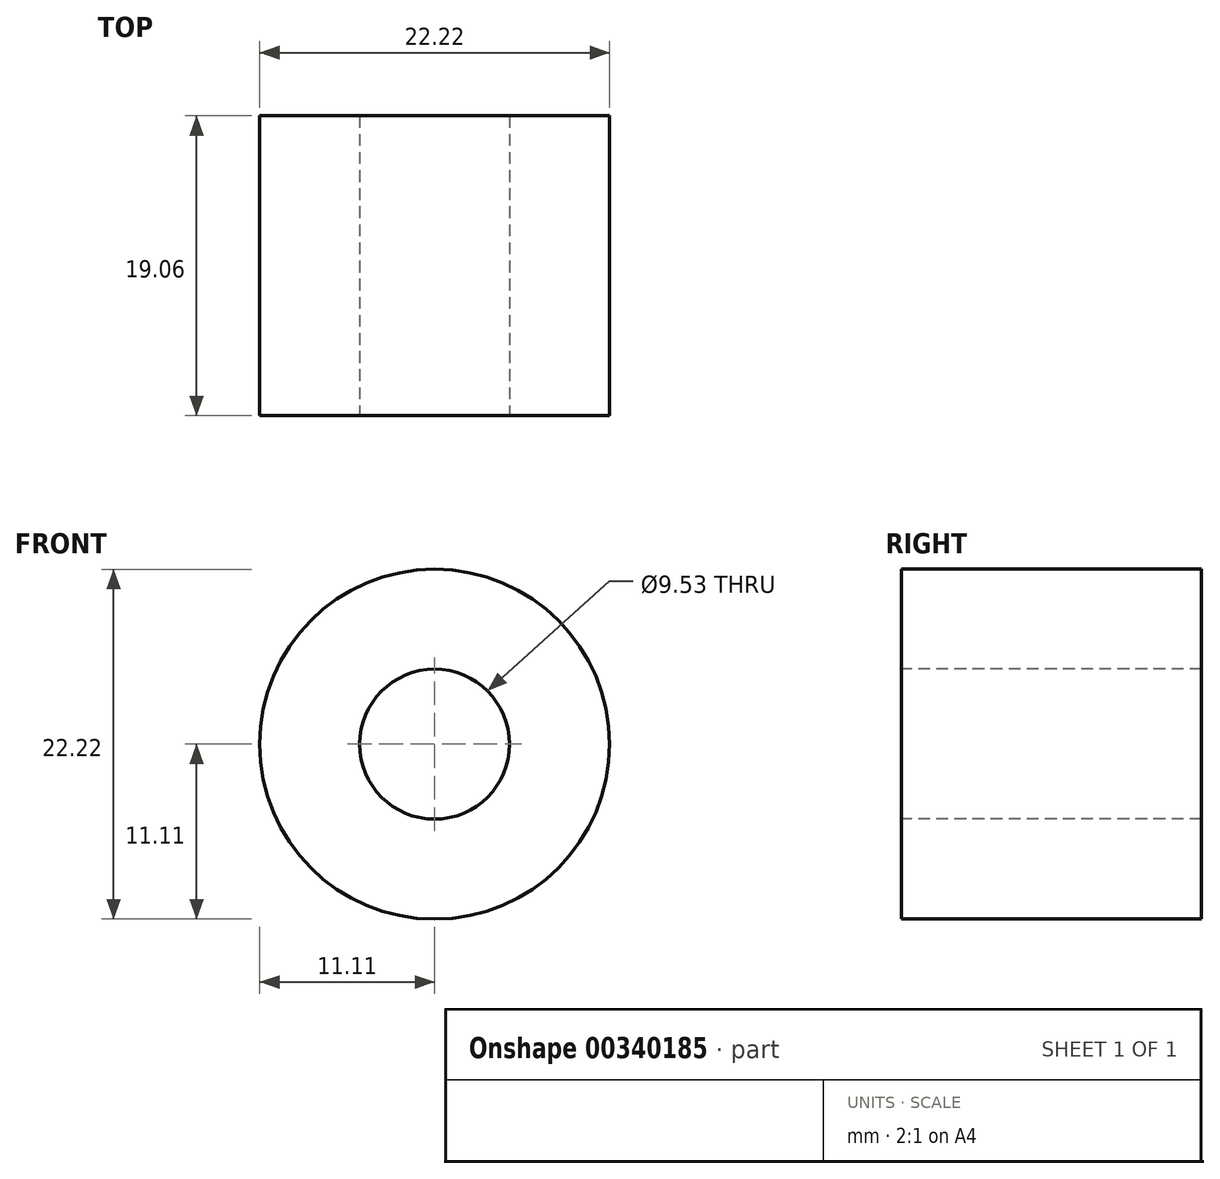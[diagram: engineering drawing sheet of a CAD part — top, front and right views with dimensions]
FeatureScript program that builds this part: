
annotation { "Feature Type Name" : "Feature", "Feature Type Description" : "" }
export const myFeature = defineFeature(function(context is Context, id is Id, definition is map)
    precondition{}
    {
        {
            var Q0;
            Q0=qCreatedBy(makeId("Top.planeOp"),FACE);
            var sketch = newSketch(context, id + "F0", { "sketchPlane" : qUnion([Q0])});
            skLineSegment(sketch, "E0", {"start": v(-4.76, 9.52) * mm, "end": v(-4.76, -9.53) * mm});
            skLineSegment(sketch, "E1", {"start": v(-4.76, 9.52) * mm, "end": v(-11.11, 9.52) * mm});
            skLineSegment(sketch, "E2", {"start": v(-11.11, 9.52) * mm, "end": v(-11.11, -9.53) * mm});
            skLineSegment(sketch, "E3", {"start": v(-11.11, -9.53) * mm, "end": v(-4.76, -9.53) * mm});
            skLineSegment(sketch, "E4", {"start": v(0, 0) * mm, "end": v(0, 14.35) * mm, "construction": true});
            skSolve(sketch);
        }
        {
            var Q0;
            Q0 = qSketchRegion(id + "F0", true);
            var Q1;
            Q1=sQuery(id+"F0.wireOp",EDGE,"E4");
            revolve(context, id + "F1", {"entities" : qUnion([Q0]), "axis" : qUnion([Q1]), "revolveType" : RevolveType.FULL});
        }
    });
